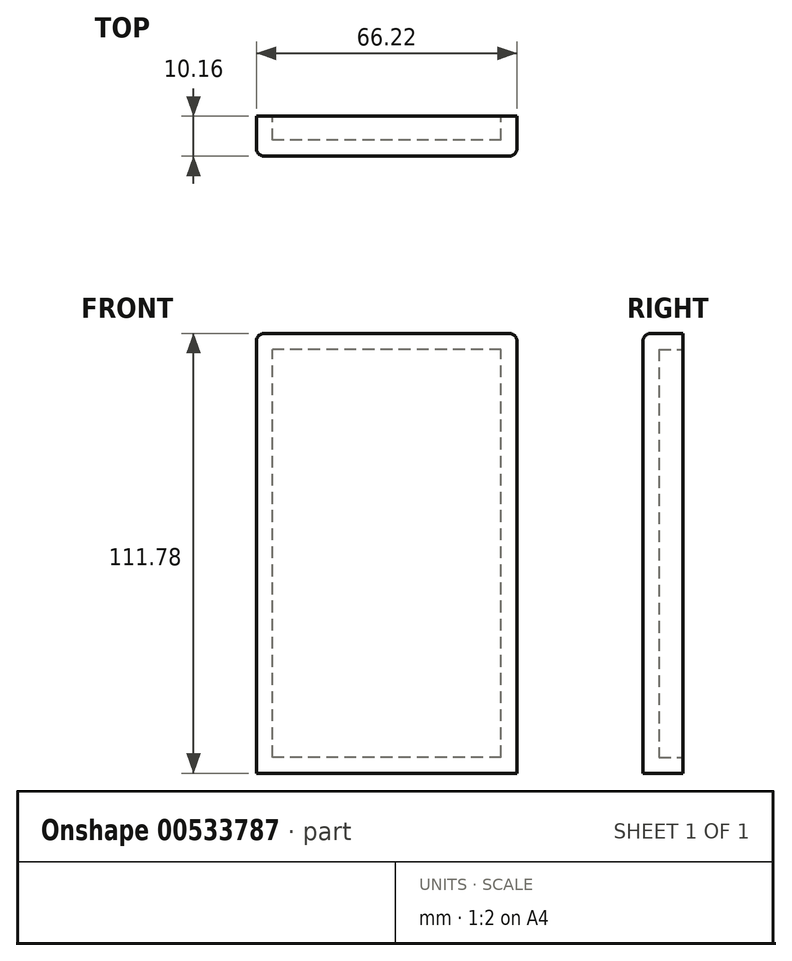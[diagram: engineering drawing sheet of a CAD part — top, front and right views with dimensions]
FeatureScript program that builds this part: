
annotation { "Feature Type Name" : "Feature", "Feature Type Description" : "" }
export const myFeature = defineFeature(function(context is Context, id is Id, definition is map)
    precondition{}
    {
        {
            var Q0;
            Q0=qCreatedBy(makeId("Front.planeOp"),FACE);
            var sketch = newSketch(context, id + "F0", { "sketchPlane" : qUnion([Q0])});
            skLineSegment(sketch, "E0.bottom", {"start": v(0, 0) * mm, "end": v(-66.22, 0) * mm});
            skLineSegment(sketch, "E0.top", {"start": v(0, 111.78) * mm, "end": v(-66.22, 111.78) * mm});
            skLineSegment(sketch, "E0.left", {"start": v(0, 0) * mm, "end": v(0, 111.78) * mm});
            skLineSegment(sketch, "E0.right", {"start": v(-66.22, 0) * mm, "end": v(-66.22, 111.78) * mm});
            skSolve(sketch);
        }
        {
            var Q0;
            Q0=makeQuery(id+"F0.imprint","IMPRINT",FACE,{"disambiguationData":[TD([[makeQuery(id+"F0.imprint","IMPRINT",EDGE,{"derivedFrom":sQuery(id+"F0.wireOp",EDGE,"E0.bottom")}),-1.0]])]});
            extrude(context, id + "F1", {"entities" : qUnion([Q0]), "depth" : 10.16 * mm, "offsetDistance" : 25.4 * mm});
        }
        {
            var Q0;
            Q0=makeQuery(id+"F1.opExtrude","CAP_EDGE",EDGE,{"disambiguationData":[OSD([sQuery(id+"F0.wireOp",EDGE,"E0.left")])],"isStart":false});
            var Q1;
            Q1=makeQuery(id+"FxPktXh6ZoMWM0g_1.opFillet","BLEND_EDGE",EDGE,{"blendedFrom":[makeQuery(id+"F1.opExtrude","CAP_EDGE",EDGE,{"disambiguationData":[OSD([sQuery(id+"F0.wireOp",EDGE,"E0.top")])],"isStart":false}),makeQuery(id+"F1.opExtrude","SWEPT_FACE",FACE,{"disambiguationData":[OSD([sQuery(id+"F0.wireOp",EDGE,"E0.left")])]})],"blendedInto":[makeQuery(id+"F1.opExtrude","SWEPT_FACE",FACE,{"disambiguationData":[OSD([sQuery(id+"F0.wireOp",EDGE,"E0.left")])]})]});
            var Q2;
            Q2=makeQuery(id+"F1.opExtrude","CAP_EDGE",EDGE,{"disambiguationData":[OSD([sQuery(id+"F0.wireOp",EDGE,"E0.right")])],"isStart":false});
            var Q3;
            Q3=makeQuery(id+"FxPktXh6ZoMWM0g_1.opFillet","BLEND_EDGE",EDGE,{"blendedFrom":[makeQuery(id+"F1.opExtrude","CAP_EDGE",EDGE,{"disambiguationData":[OSD([sQuery(id+"F0.wireOp",EDGE,"E0.top")])],"isStart":false}),makeQuery(id+"F1.opExtrude","SWEPT_FACE",FACE,{"disambiguationData":[OSD([sQuery(id+"F0.wireOp",EDGE,"E0.right")])]})],"blendedInto":[makeQuery(id+"F1.opExtrude","SWEPT_FACE",FACE,{"disambiguationData":[OSD([sQuery(id+"F0.wireOp",EDGE,"E0.right")])]})]});
            fillet(context, id + "F2", {"entities" : qUnion([Q0, Q1, Q2, Q3]), "radius" : 2.03 * mm, "tangentPropagation" : true, "allowEdgeOverflow" : false});
        }
        {
            var Q0;
            Q0=makeQuery(id+"F1.opExtrude","CAP_FACE",FACE,{"disambiguationData":[OSD([sQuery(id+"F0.wireOp",EDGE,"E0.bottom"),sQuery(id+"F0.wireOp",EDGE,"E0.top"),sQuery(id+"F0.wireOp",EDGE,"E0.left"),sQuery(id+"F0.wireOp",EDGE,"E0.right")])],"isStart":true});
            shell(context, id + "F3", {"entities" : qUnion([Q0]), "thickness" : 4.06 * mm});
        }
        {
            var Q0;
            Q0=makeQuery(id+"F1.opExtrude","SWEPT_EDGE",EDGE,{"disambiguationData":[OSD([sQuery(id+"F0.wireOp",EDGE,"E0.top"),sQuery(id+"F0.wireOp",EDGE,"E0.right")])]});
            fillet(context, id + "F4", {"entities" : qUnion([Q0]), "radius" : 2.03 * mm, "tangentPropagation" : true, "allowEdgeOverflow" : false});
        }
    });
